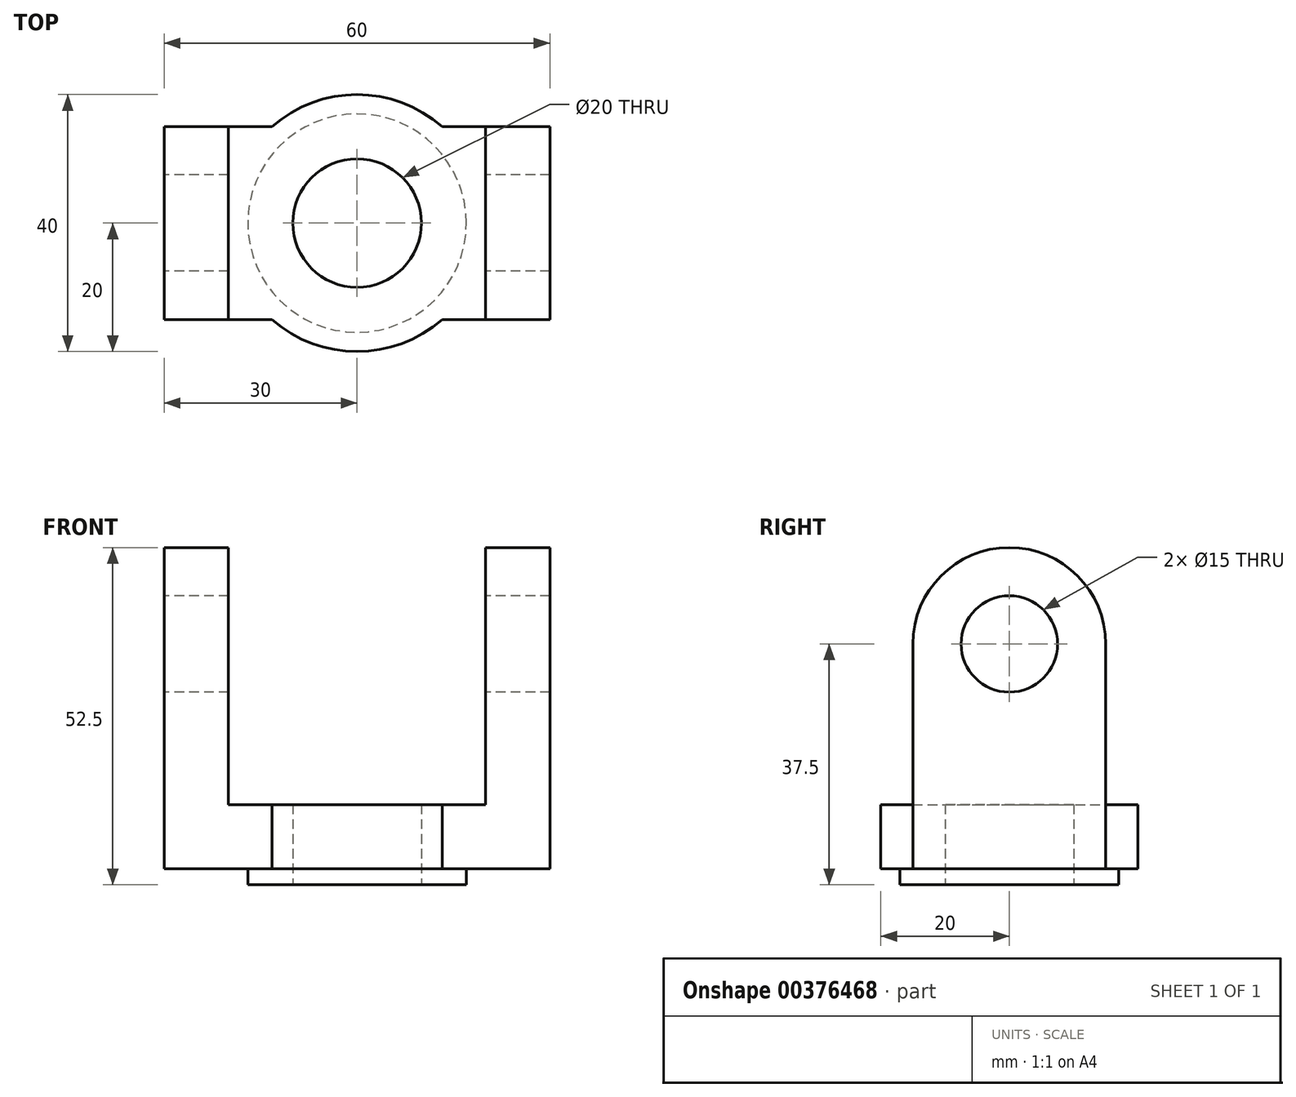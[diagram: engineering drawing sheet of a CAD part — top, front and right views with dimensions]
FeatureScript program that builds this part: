
annotation { "Feature Type Name" : "Feature", "Feature Type Description" : "" }
export const myFeature = defineFeature(function(context is Context, id is Id, definition is map)
    precondition{}
    {
        {
            var Q0;
            Q0=qCreatedBy(makeId("Right.planeOp"),FACE);
            var sketch = newSketch(context, id + "F0", { "sketchPlane" : qUnion([Q0])});
            skLineSegment(sketch, "E0", {"start": v(-15, 0) * mm, "end": v(15, 0) * mm});
            skLineSegment(sketch, "E1", {"start": v(15, 0) * mm, "end": v(15, 35) * mm});
            skLineSegment(sketch, "E2", {"start": v(-15, 0) * mm, "end": v(-15, 35) * mm});
            skCircle(sketch, "E3", {"center": v(0, 35) * mm, "radius": 7.5 * mm});
            skArc(sketch, "E4", {"start": v(15, 35) * mm, "mid": v(0, 50) * mm, "end": v(-15, 35) * mm});
            skSolve(sketch);
        }
        {
            var Q0;
            Q0 = qSketchRegion(id + "F0", true);
            extrude(context, id + "F1", {"entities" : qUnion([Q0]), "endBound" : BoundingType.SYMMETRIC, "depth" : 60 * mm});
        }
        {
            var Q0;
            Q0=qCreatedBy(makeId("Front.planeOp"),FACE);
            var sketch = newSketch(context, id + "F2", { "sketchPlane" : qUnion([Q0])});
            skLineSegment(sketch, "E5", {"start": v(-20, 10) * mm, "end": v(20, 10) * mm});
            skLineSegment(sketch, "E6", {"start": v(20, 10) * mm, "end": v(20, 50) * mm});
            skLineSegment(sketch, "E7", {"start": v(20, 50) * mm, "end": v(-20, 50) * mm});
            skLineSegment(sketch, "E8", {"start": v(-20, 50) * mm, "end": v(-20, 10) * mm});
            skSolve(sketch);
        }
        {
            var Q0;
            Q0 = qSketchRegion(id + "F2", true);
            extrude(context, id + "F3", {"entities" : qUnion([Q0]), "operationType" : NewBodyOperationType.REMOVE, "depth" : 25 * mm, "hasSecondDirection" : true, "secondDirectionOppositeDirection" : true, "secondDirectionDepth" : 25 * mm});
        }
        {
            var Q0;
            Q0=qCreatedBy(makeId("Top.planeOp"),FACE);
            var sketch = newSketch(context, id + "F4", { "sketchPlane" : qUnion([Q0])});
            skCircle(sketch, "E9", {"center": v(0, 0) * mm, "radius": 20 * mm});
            skSolve(sketch);
        }
        {
            var Q0;
            Q0 = qSketchRegion(id + "F4", true);
            extrude(context, id + "F5", {"entities" : qUnion([Q0]), "operationType" : NewBodyOperationType.ADD, "depth" : 10 * mm});
        }
        {
            var Q0;
            Q0=qCreatedBy(makeId("Top.planeOp"),FACE);
            var sketch = newSketch(context, id + "F6", { "sketchPlane" : qUnion([Q0])});
            skCircle(sketch, "E10", {"center": v(0, 0) * mm, "radius": 10 * mm});
            skSolve(sketch);
        }
        {
            var Q0;
            Q0 = qSketchRegion(id + "F6", true);
            extrude(context, id + "F7", {"entities" : qUnion([Q0]), "operationType" : NewBodyOperationType.REMOVE, "endBound" : BoundingType.THROUGH_ALL, "depth" : 25 * mm, "hasSecondDirection" : true, "secondDirectionOppositeDirection" : true, "secondDirectionDepth" : 25 * mm});
        }
        {
            var Q0;
            Q0=qCreatedBy(makeId("Top.planeOp"),FACE);
            var sketch = newSketch(context, id + "F8", { "sketchPlane" : qUnion([Q0])});
            skCircle(sketch, "E11", {"center": v(0, 0) * mm, "radius": 17 * mm});
            skSolve(sketch);
        }
        {
            var Q0;
            Q0 = qSketchRegion(id + "F8", true);
            extrude(context, id + "F9", {"entities" : qUnion([Q0]), "operationType" : NewBodyOperationType.ADD, "oppositeDirection" : true, "depth" : 2.5 * mm});
        }
        {
            var Q0;
            Q0=makeQuery(id+"F6.imprint","IMPRINT",FACE,{"disambiguationData":[TD([[makeQuery(id+"F6.imprint","IMPRINT",EDGE,{"derivedFrom":sQuery(id+"F6.wireOp",EDGE,"E10")}),1.0]])]});
            extrude(context, id + "F10", {"entities" : qUnion([Q0]), "operationType" : NewBodyOperationType.REMOVE, "oppositeDirection" : true, "depth" : 25 * mm});
        }
    });
